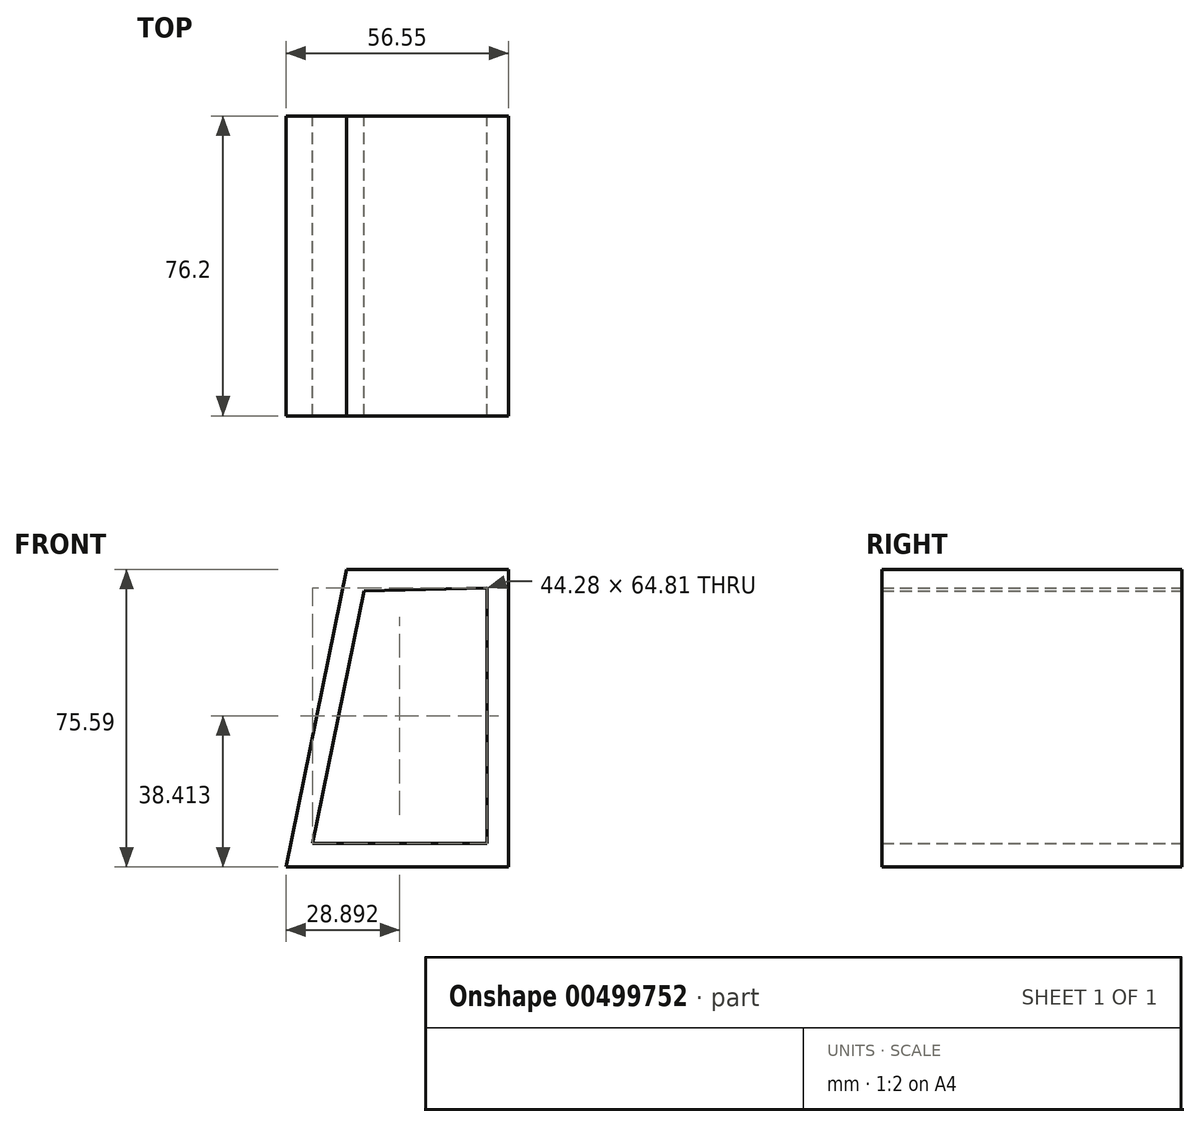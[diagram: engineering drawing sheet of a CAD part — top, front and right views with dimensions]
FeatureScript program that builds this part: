
annotation { "Feature Type Name" : "Feature", "Feature Type Description" : "" }
export const myFeature = defineFeature(function(context is Context, id is Id, definition is map)
    precondition{}
    {
        {
            var Q0;
            Q0=qCreatedBy(makeId("Front.planeOp"),FACE);
            var sketch = newSketch(context, id + "F0", { "sketchPlane" : qUnion([Q0])});
            skLineSegment(sketch, "E0", {"start": v(-40.14, 24.36) * mm, "end": v(1, 24.36) * mm});
            skLineSegment(sketch, "E1", {"start": v(-40.14, 24.36) * mm, "end": v(-40.14, -51.23) * mm});
            skLineSegment(sketch, "E2", {"start": v(1, 24.36) * mm, "end": v(1, -51.23) * mm});
            skLineSegment(sketch, "E3", {"start": v(-40.14, -51.23) * mm, "end": v(1, -51.23) * mm});
            skLineSegment(sketch, "E4", {"start": v(-40.14, 24.36) * mm, "end": v(1, -51.23) * mm});
            skLineSegment(sketch, "E5", {"start": v(-55.55, -51.23) * mm, "end": v(-40.14, 24.36) * mm});
            skLineSegment(sketch, "E6", {"start": v(-55.55, -51.23) * mm, "end": v(-40.14, -51.23) * mm});
            skLineSegment(sketch, "E7", {"start": v(-55.55, -51.23) * mm, "end": v(1, 24.36) * mm});
            skLineSegment(sketch, "E8", {"start": v(1, 24.36) * mm, "end": v(-14.4, -51.23) * mm});
            skSolve(sketch);
        }
        {
            var Q0;
            {var subQ5=sQuery(id+"F0.wireOp",EDGE,"E4");var subQ7=sQuery(id+"F0.wireOp",EDGE,"E7");var subQ9=makeQuery(id+"F0.imprint","INTERSECT",VERTEX,{"derivedFrom":[subQ5,subQ7]});Q0=makeQuery(id+"F0.imprint","IMPRINT",FACE,{"disambiguationData":[TD([[makeQuery(id+"F0.imprint","IMPRINT",EDGE,{"disambiguationData":[TD([[subQ9,-1.0]])],"derivedFrom":subQ5}),-1.0]])]});}
            var Q1;
            {var subQ1=sQuery(id+"F0.wireOp",EDGE,"E3");var subQ3=sQuery(id+"F0.wireOp",EDGE,"E8");var subQ4=makeQuery(id+"F0.imprint","INTERSECT",VERTEX,{"derivedFrom":[subQ1,subQ3]});Q1=makeQuery(id+"F0.imprint","IMPRINT",FACE,{"disambiguationData":[TD([[makeQuery(id+"F0.imprint","IMPRINT",EDGE,{"disambiguationData":[TD([[subQ4,1.0]])],"derivedFrom":subQ3}),1.0]])]});}
            var Q2;
            {var subQ0=sQuery(id+"F0.wireOp",EDGE,"E2");Q2=makeQuery(id+"F0.imprint","IMPRINT",FACE,{"disambiguationData":[TD([[makeQuery(id+"F0.imprint","IMPRINT",EDGE,{"derivedFrom":subQ0}),-1.0]])]});}
            var Q3;
            {var subQ0=sQuery(id+"F0.wireOp",EDGE,"E7");var subQ1=sQuery(id+"F0.wireOp",EDGE,"E4");var subQ2=makeQuery(id+"F0.imprint","INTERSECT",VERTEX,{"derivedFrom":[subQ1,subQ0]});Q3=makeQuery(id+"F0.imprint","IMPRINT",FACE,{"disambiguationData":[TD([[makeQuery(id+"F0.imprint","IMPRINT",EDGE,{"disambiguationData":[TD([[subQ2,-1.0]])],"derivedFrom":subQ1}),1.0]])]});}
            var Q4;
            {var subQ0=sQuery(id+"F0.wireOp",EDGE,"E0");Q4=makeQuery(id+"F0.imprint","IMPRINT",FACE,{"disambiguationData":[TD([[makeQuery(id+"F0.imprint","IMPRINT",EDGE,{"derivedFrom":subQ0}),-1.0]])]});}
            var Q5;
            {var subQ1=sQuery(id+"F0.wireOp",EDGE,"E1");var subQ3=sQuery(id+"F0.wireOp",EDGE,"E7");var subQ4=makeQuery(id+"F0.imprint","INTERSECT",VERTEX,{"derivedFrom":[subQ1,subQ3]});Q5=makeQuery(id+"F0.imprint","IMPRINT",FACE,{"disambiguationData":[TD([[makeQuery(id+"F0.imprint","IMPRINT",EDGE,{"disambiguationData":[TD([[subQ4,-1.0]])],"derivedFrom":subQ3}),1.0]])]});}
            var Q6;
            {var subQ0=sQuery(id+"F0.wireOp",EDGE,"E6");Q6=makeQuery(id+"F0.imprint","IMPRINT",FACE,{"disambiguationData":[TD([[makeQuery(id+"F0.imprint","IMPRINT",EDGE,{"derivedFrom":subQ0}),1.0]])]});}
            var Q7;
            {var subQ0=sQuery(id+"F0.wireOp",EDGE,"E5");Q7=makeQuery(id+"F0.imprint","IMPRINT",FACE,{"disambiguationData":[TD([[makeQuery(id+"F0.imprint","IMPRINT",EDGE,{"derivedFrom":subQ0}),-1.0]])]});}
            extrude(context, id + "F1", {"entities" : qUnion([Q0, Q1, Q2, Q3, Q4, Q5, Q6, Q7]), "depth" : 76.2 * mm});
        }
        {
            var Q0;
            Q0=makeQuery(id+"F1.opExtrude","CAP_FACE",FACE,{"disambiguationData":[OSD([sQuery(id+"F0.wireOp",EDGE,"E0"),sQuery(id+"F0.wireOp",EDGE,"E2"),sQuery(id+"F0.wireOp",EDGE,"E3"),sQuery(id+"F0.wireOp",EDGE,"E5"),sQuery(id+"F0.wireOp",EDGE,"E6")])],"isStart":true});
            var sketch = newSketch(context, id + "F2", { "sketchPlane" : qUnion([Q0])});
            skLineSegment(sketch, "E9", {"start": v(4.52, 19.6) * mm, "end": v(4.52, -45.22) * mm});
            skLineSegment(sketch, "E10", {"start": v(4.52, -45.22) * mm, "end": v(48.8, -45.22) * mm});
            skLineSegment(sketch, "E11", {"start": v(48.8, -45.22) * mm, "end": v(35.74, 18.88) * mm});
            skLineSegment(sketch, "E12", {"start": v(35.74, 18.88) * mm, "end": v(4.52, 19.6) * mm});
            skSolve(sketch);
        }
        {
            var Q0;
            Q0=makeQuery(id+"F2.imprint","IMPRINT",FACE,{"disambiguationData":[TD([[makeQuery(id+"F2.imprint","IMPRINT",EDGE,{"derivedFrom":sQuery(id+"F2.wireOp",EDGE,"E9")}),1.0]])]});
            extrude(context, id + "F3", {"entities" : qUnion([Q0]), "operationType" : NewBodyOperationType.REMOVE, "oppositeDirection" : true, "depth" : 76.2 * mm});
        }
    });
